# Revit family: Ballu ASP 100
name_source: partatom
category: Воздухораспределители
units: mm (PartAtom-declared; Revit-internal decimal feet)

## family parameters
Всегда вертикально = Да
На основе рабочей плоскости = Нет
Общий = Нет
При загрузке вырезать с полостями = Нет
Размер круглого соединителя = Использовать диаметр
Тип детали = Нормальный
Точка расчета площади = Нет

## types (1)
- Ballu ONEAIR - 100
    ADSK_Версия Revit = 2019
    ADSK_Версия семейства = 1
    ADSK_Единица измерения = шт.
    ADSK_Завод-изготовитель = Фошан БИГ Климатик Мануфактуре Ко. ЛТД, Жонгшан Бранч
    ADSK_Классификация нагрузок = ОВК
    ADSK_Код изделия = ASP-100
    ADSK_Количество = 1
    ADSK_Количество фаз = 1
    ADSK_Количество фаз числовое = 1
    ADSK_Коэффициент мощности = 0.95
    ADSK_Марка = Ballu
    ADSK_Масса = 3.5
    ADSK_Масса_Текст = 3.5
    ADSK_Материал = Пластмасса, непрозрачная, белая
    ADSK_Наименование = Очиститель воздуха приточный Ballu ONEAIR ASP-100
    ADSK_Наименование краткое = Ballu ASP-100
    ADSK_Напряжение = 220 В
    ADSK_Номинальная мощность = 24 Вт
    ADSK_Полная мощность = 25 В·А
    ADSK_Размер_Высота = 352 мм
    ADSK_Размер_Глубина = 160 мм
    ADSK_Размер_Диаметр = 98 мм
    ADSK_Размер_Ширина = 264 мм
    ADSK_Ток = 0 А
    URL = https://oneair.ballu.ru
    h1 = 84 мм
    Изготовитель = ООО ''Р-Климат''
